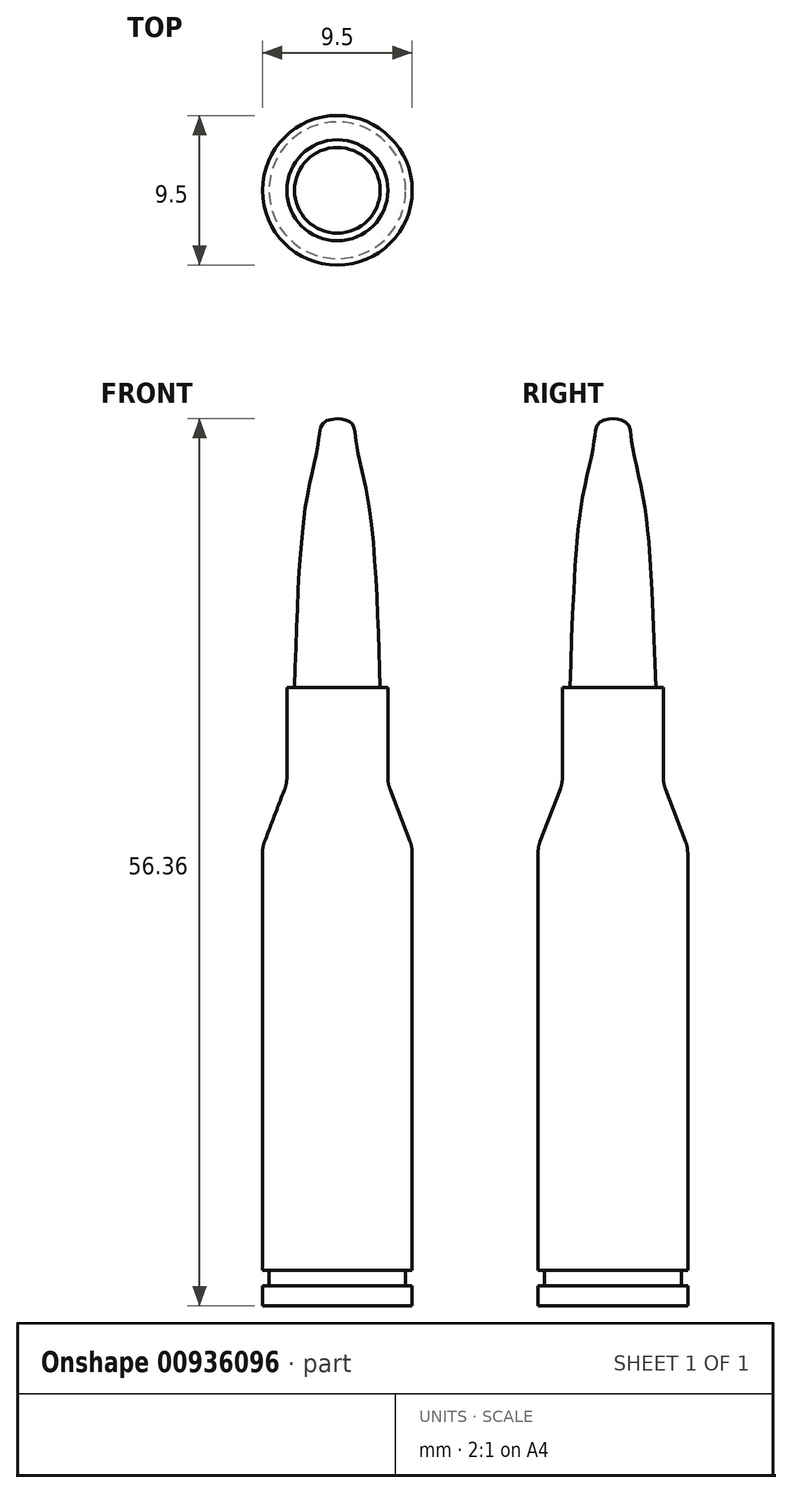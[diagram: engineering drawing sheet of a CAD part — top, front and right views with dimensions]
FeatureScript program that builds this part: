
annotation { "Feature Type Name" : "Feature", "Feature Type Description" : "" }
export const myFeature = defineFeature(function(context is Context, id is Id, definition is map)
    precondition{}
    {
        {
            var Q0;
            Q0=qCreatedBy(makeId("Front.planeOp"),FACE);
            var sketch = newSketch(context, id + "F0", { "sketchPlane" : qUnion([Q0])});
            skLineSegment(sketch, "E0", {"start": v(0, 0) * mm, "end": v(0, 59.9) * mm, "construction": true});
            skFitSpline(sketch, "E1", {"points": [v(0, 58.53) * mm, v(-0.92, 58.23) * mm, v(-1.22, 56.88) * mm, v(-1.97, 53.28) * mm, v(-2.72, 41.46) * mm], "startDerivative": vector(-8.31, -0.93) * mm, "endDerivative": vector(-0.93, -29.3) * mm});
            skLineSegment(sketch, "E2", {"start": v(-2.72, 41.46) * mm, "end": v(0, 41.46) * mm});
            skLineSegment(sketch, "E3", {"start": v(-2.72, 41.46) * mm, "end": v(-3.2, 41.46) * mm});
            skLineSegment(sketch, "E4", {"start": v(-3.2, 41.46) * mm, "end": v(-3.2, 35.37) * mm});
            skLineSegment(sketch, "E5", {"start": v(-3.2, 35.37) * mm, "end": v(-4.75, 31.32) * mm});
            skLineSegment(sketch, "E6", {"start": v(-4.75, 31.32) * mm, "end": v(-4.75, 4.42) * mm});
            skLineSegment(sketch, "E7", {"start": v(-4.75, 4.42) * mm, "end": v(0, 4.42) * mm});
            skLineSegment(sketch, "E8", {"start": v(-4.34, 4.42) * mm, "end": v(-4.34, 3.45) * mm});
            skLineSegment(sketch, "E9", {"start": v(-4.34, 3.45) * mm, "end": v(-4.75, 3.45) * mm});
            skLineSegment(sketch, "E10", {"start": v(-4.75, 3.45) * mm, "end": v(-4.75, 2.17) * mm});
            skLineSegment(sketch, "E11", {"start": v(-4.75, 2.17) * mm, "end": v(0, 2.17) * mm});
            skLineSegment(sketch, "E12", {"start": v(-4.34, 3.45) * mm, "end": v(0, 3.45) * mm});
            skLineSegment(sketch, "E13", {"start": v(0, 3.45) * mm, "end": v(0, 4.42) * mm});
            skLineSegment(sketch, "E14", {"start": v(0, 2.17) * mm, "end": v(0, 3.45) * mm});
            skLineSegment(sketch, "E15", {"start": v(0, 4.42) * mm, "end": v(0, 41.46) * mm});
            skLineSegment(sketch, "E16", {"start": v(0, 58.53) * mm, "end": v(0, 41.46) * mm});
            skSolve(sketch);
        }
        {
            var Q0;
            Q0=makeQuery(id+"F0.imprint","IMPRINT",FACE,{"disambiguationData":[TD([[makeQuery(id+"F0.imprint","IMPRINT",EDGE,{"derivedFrom":sQuery(id+"F0.wireOp",EDGE,"E2")}),-1.0]])]});
            var Q1;
            {var subQ2=sQuery(id+"F0.wireOp",EDGE,"E8");Q1=makeQuery(id+"F0.imprint","IMPRINT",FACE,{"disambiguationData":[TD([[makeQuery(id+"F0.imprint","IMPRINT",EDGE,{"derivedFrom":subQ2}),1.0]])]});}
            var Q2;
            Q2=makeQuery(id+"F0.imprint","IMPRINT",FACE,{"disambiguationData":[TD([[makeQuery(id+"F0.imprint","IMPRINT",EDGE,{"derivedFrom":sQuery(id+"F0.wireOp",EDGE,"E9")}),1.0]])]});
            var Q3;
            Q3=sQuery(id+"F0.wireOp",EDGE,"E1");
            var Q4;
            Q4=sQuery(id+"F0.wireOp",EDGE,"E4");
            var Q5;
            Q5=sQuery(id+"F0.wireOp",EDGE,"E5");
            var Q6;
            Q6=sQuery(id+"F0.wireOp",EDGE,"E6");
            var Q7;
            Q7=sQuery(id+"F0.wireOp",EDGE,"E8");
            var Q8;
            Q8=sQuery(id+"F0.wireOp",EDGE,"E10");
            var Q9;
            Q9=sQuery(id+"F0.wireOp",EDGE,"E0");
            revolve(context, id + "F1", {"entities" : qUnion([Q0, Q1, Q2]), "surfaceEntities" : qUnion([Q3, Q4, Q5, Q6, Q7, Q8]), "axis" : qUnion([Q9]), "revolveType" : RevolveType.FULL});
        }
        {
            var Q0;
            Q0=makeQuery(id+"F1.opRevolve","SWEPT_EDGE",EDGE,{"disambiguationData":[OSD([sQuery(id+"F0.wireOp",EDGE,"E4"),sQuery(id+"F0.wireOp",EDGE,"E5")])]});
            var Q1;
            Q1=makeQuery(id+"F1.opRevolve","SWEPT_EDGE",EDGE,{"disambiguationData":[OSD([sQuery(id+"F0.wireOp",EDGE,"E5"),sQuery(id+"F0.wireOp",EDGE,"E6")])]});
            fillet(context, id + "F2", {"entities" : qUnion([Q0, Q1]), "radius" : 2 * mm, "tangentPropagation" : true, "allowEdgeOverflow" : false});
        }
        {
            var Q0;
            Q0=makeQuery(id+"F0.imprint","IMPRINT",FACE,{"disambiguationData":[TD([[makeQuery(id+"F0.imprint","IMPRINT",EDGE,{"derivedFrom":sQuery(id+"F0.wireOp",EDGE,"E1")}),1.0]])]});
            var Q1;
            Q1=sQuery(id+"F0.wireOp",EDGE,"E0");
            revolve(context, id + "F3", {"entities" : qUnion([Q0]), "axis" : qUnion([Q1]), "revolveType" : RevolveType.FULL});
        }
    });
